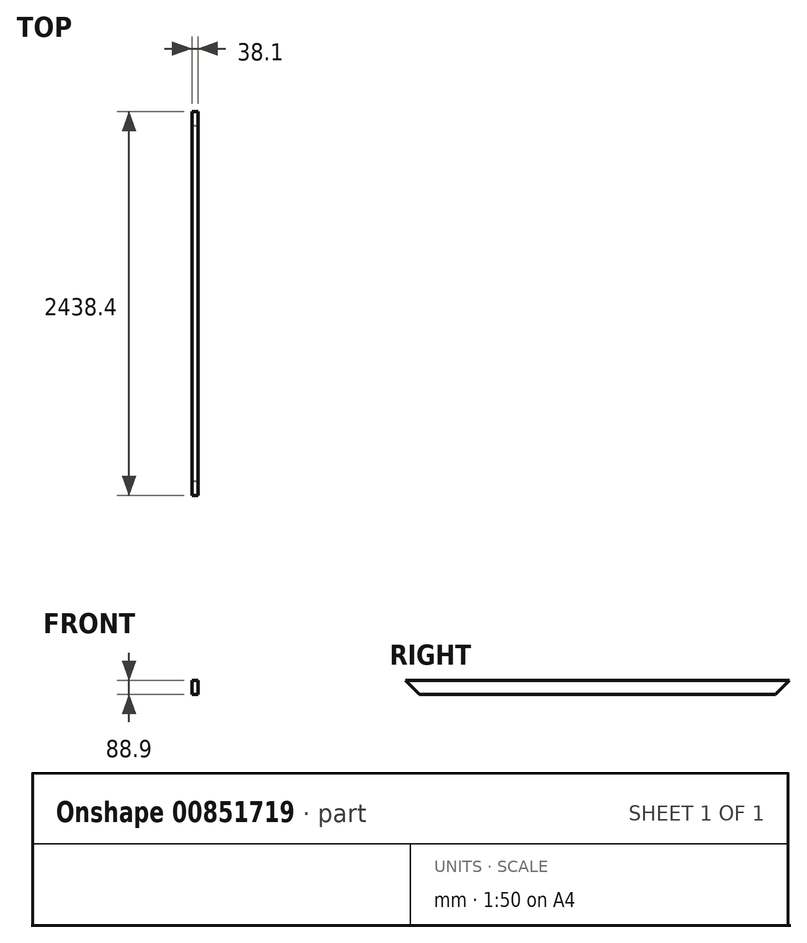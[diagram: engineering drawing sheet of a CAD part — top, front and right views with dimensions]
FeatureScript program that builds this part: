
annotation { "Feature Type Name" : "Feature", "Feature Type Description" : "" }
export const myFeature = defineFeature(function(context is Context, id is Id, definition is map)
    precondition{}
    {
        {
            var Q0;
            Q0=qCreatedBy(makeId("Front.planeOp"),FACE);
            var sketch = newSketch(context, id + "F0", { "sketchPlane" : qUnion([Q0])});
            skLineSegment(sketch, "E0.bottom", {"start": v(-19.05, 44.45) * mm, "end": v(19.05, 44.45) * mm});
            skLineSegment(sketch, "E0.top", {"start": v(-19.05, -44.45) * mm, "end": v(19.05, -44.45) * mm});
            skLineSegment(sketch, "E0.left", {"start": v(-19.05, 44.45) * mm, "end": v(-19.05, -44.45) * mm});
            skLineSegment(sketch, "E0.right", {"start": v(19.05, 44.45) * mm, "end": v(19.05, -44.45) * mm});
            skPoint(sketch, "E0.middle", {"position": v(0, 0) * mm});
            skSolve(sketch);
        }
        {
            var Q0;
            Q0=makeQuery(id+"F0.imprint","IMPRINT",FACE,{"disambiguationData":[TD([[makeQuery(id+"F0.imprint","IMPRINT",EDGE,{"derivedFrom":sQuery(id+"F0.wireOp",EDGE,"E0.bottom")}),-1.0]])]});
            extrude(context, id + "F1", {"entities" : qUnion([Q0]), "endBound" : BoundingType.SYMMETRIC, "depth" : 2438.4 * mm, "offsetDistance" : 25.4 * mm});
        }
        {
            var Q0;
            Q0=makeQuery(id+"F1.opExtrude","CAP_EDGE",EDGE,{"disambiguationData":[OSD([sQuery(id+"F0.wireOp",EDGE,"E0.top")])],"isStart":false});
            chamfer(context, id + "F2", {"entities" : qUnion([Q0]), "chamferType" : ChamferType.TWO_OFFSETS, "width1" : 88.9 * mm, "oppositeDirection" : false, "width2" : 88.9 * mm, "tangentPropagation" : true});
        }
        {
            var Q0;
            Q0=makeQuery(id+"F1.opExtrude","CAP_EDGE",EDGE,{"disambiguationData":[OSD([sQuery(id+"F0.wireOp",EDGE,"E0.top")])],"isStart":true});
            chamfer(context, id + "F3", {"entities" : qUnion([Q0]), "chamferType" : ChamferType.TWO_OFFSETS, "width1" : 88.9 * mm, "oppositeDirection" : false, "width2" : 88.9 * mm, "tangentPropagation" : true});
        }
    });
